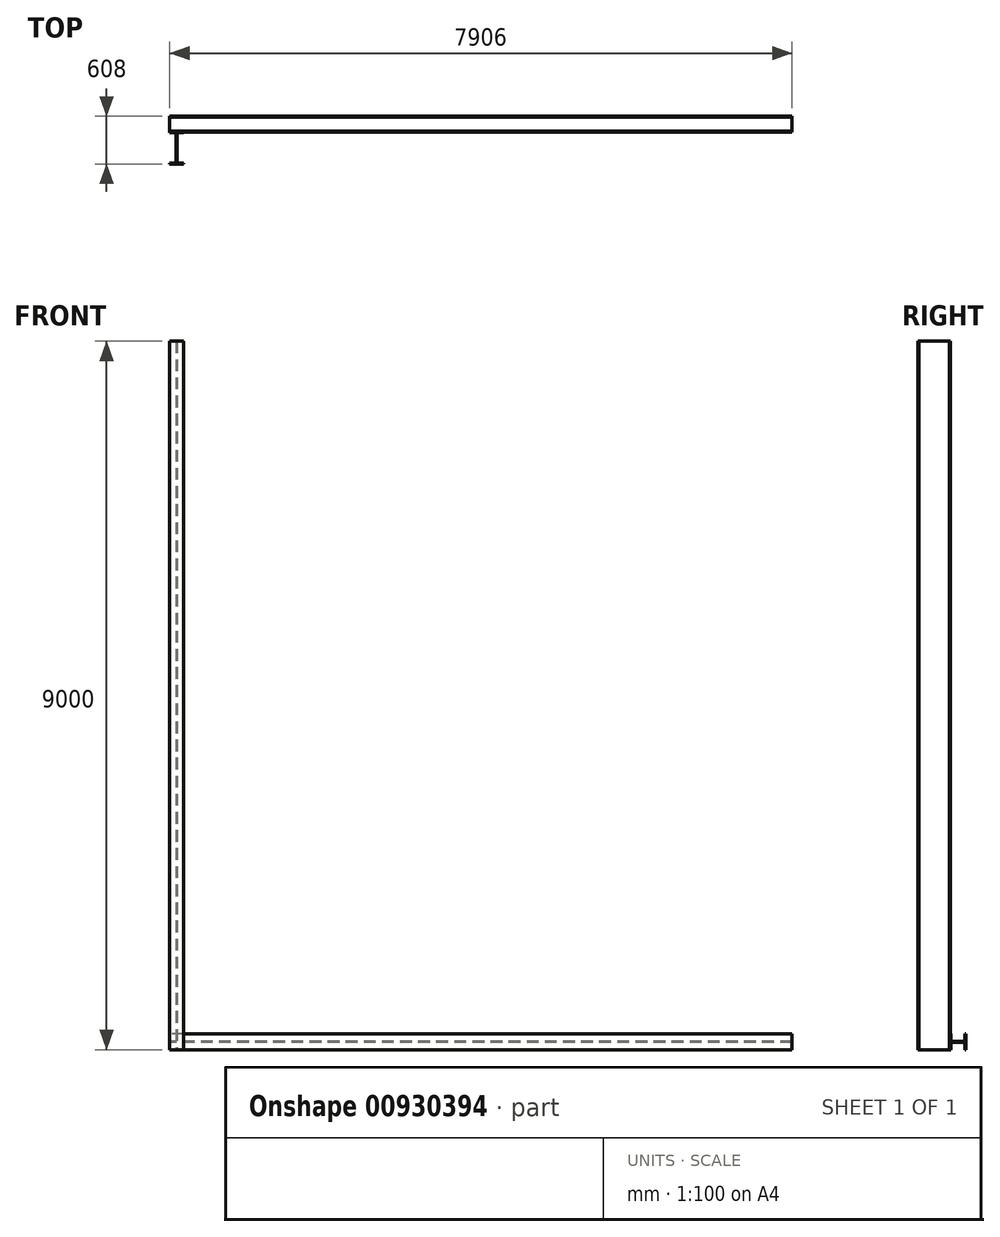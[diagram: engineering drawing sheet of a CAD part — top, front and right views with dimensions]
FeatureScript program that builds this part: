
annotation { "Feature Type Name" : "Feature", "Feature Type Description" : "" }
export const myFeature = defineFeature(function(context is Context, id is Id, definition is map)
    precondition{}
    {
        {
            var Q0;
            Q0=qCreatedBy(makeId("Top.planeOp"),FACE);
            var sketch = newSketch(context, id + "F0", { "sketchPlane" : qUnion([Q0])});
            skLineSegment(sketch, "E0", {"start": v(0, 0) * mm, "end": v(178, 0) * mm});
            skLineSegment(sketch, "E1", {"start": v(178, 0) * mm, "end": v(178, -10) * mm});
            skLineSegment(sketch, "E2", {"start": v(178, -10) * mm, "end": v(94, -10) * mm});
            skLineSegment(sketch, "E3", {"start": v(94, -10) * mm, "end": v(94, -398) * mm});
            skLineSegment(sketch, "E4", {"start": v(94, -398) * mm, "end": v(178, -398) * mm});
            skLineSegment(sketch, "E5", {"start": v(178, -398) * mm, "end": v(178, -408) * mm});
            skLineSegment(sketch, "E6", {"start": v(178, -408) * mm, "end": v(0, -408) * mm});
            skLineSegment(sketch, "E7", {"start": v(0, -408) * mm, "end": v(0, -398) * mm});
            skLineSegment(sketch, "E8", {"start": v(0, -398) * mm, "end": v(84, -398) * mm});
            skLineSegment(sketch, "E9", {"start": v(84, -398) * mm, "end": v(84, -10) * mm});
            skLineSegment(sketch, "E10", {"start": v(84, -10) * mm, "end": v(0, -10) * mm});
            skLineSegment(sketch, "E11", {"start": v(0, -10) * mm, "end": v(0, 0) * mm});
            skSolve(sketch);
        }
        {
            var Q0;
            Q0=qCreatedBy(makeId("Right.planeOp"),FACE);
            var sketch = newSketch(context, id + "F1", { "sketchPlane" : qUnion([Q0])});
            skLineSegment(sketch, "E12", {"start": v(0, 0) * mm, "end": v(0, 200) * mm});
            skLineSegment(sketch, "E13", {"start": v(0, 200) * mm, "end": v(10, 200) * mm});
            skLineSegment(sketch, "E14", {"start": v(10, 200) * mm, "end": v(10, 105) * mm});
            skLineSegment(sketch, "E15", {"start": v(10, 105) * mm, "end": v(190, 105) * mm});
            skLineSegment(sketch, "E16", {"start": v(190, 105) * mm, "end": v(190, 200) * mm});
            skLineSegment(sketch, "E17", {"start": v(190, 200) * mm, "end": v(200, 200) * mm});
            skLineSegment(sketch, "E18", {"start": v(200, 200) * mm, "end": v(200, 0) * mm});
            skLineSegment(sketch, "E19", {"start": v(200, 0) * mm, "end": v(190, 0) * mm});
            skLineSegment(sketch, "E20", {"start": v(190, 0) * mm, "end": v(190, 95) * mm});
            skLineSegment(sketch, "E21", {"start": v(190, 95) * mm, "end": v(10, 95) * mm});
            skLineSegment(sketch, "E22", {"start": v(10, 95) * mm, "end": v(10, 0) * mm});
            skLineSegment(sketch, "E23", {"start": v(10, 0) * mm, "end": v(0, 0) * mm});
            skSolve(sketch);
        }
        {
            var Q0;
            Q0 = qSketchRegion(id + "F0", true);
            extrude(context, id + "F2", {"entities" : qUnion([Q0]), "depth" : 9000 * mm, "offsetDistance" : 25 * mm});
        }
        {
            var Q0;
            Q0=makeQuery(id+"F1.imprint","IMPRINT",FACE,{"disambiguationData":[TD([[makeQuery(id+"F1.imprint","IMPRINT",EDGE,{"derivedFrom":sQuery(id+"F1.wireOp",EDGE,"E12")}),-1.0]])]});
            extrude(context, id + "F3", {"entities" : qUnion([Q0]), "depth" : 7906 * mm, "offsetDistance" : 25 * mm});
        }
    });
